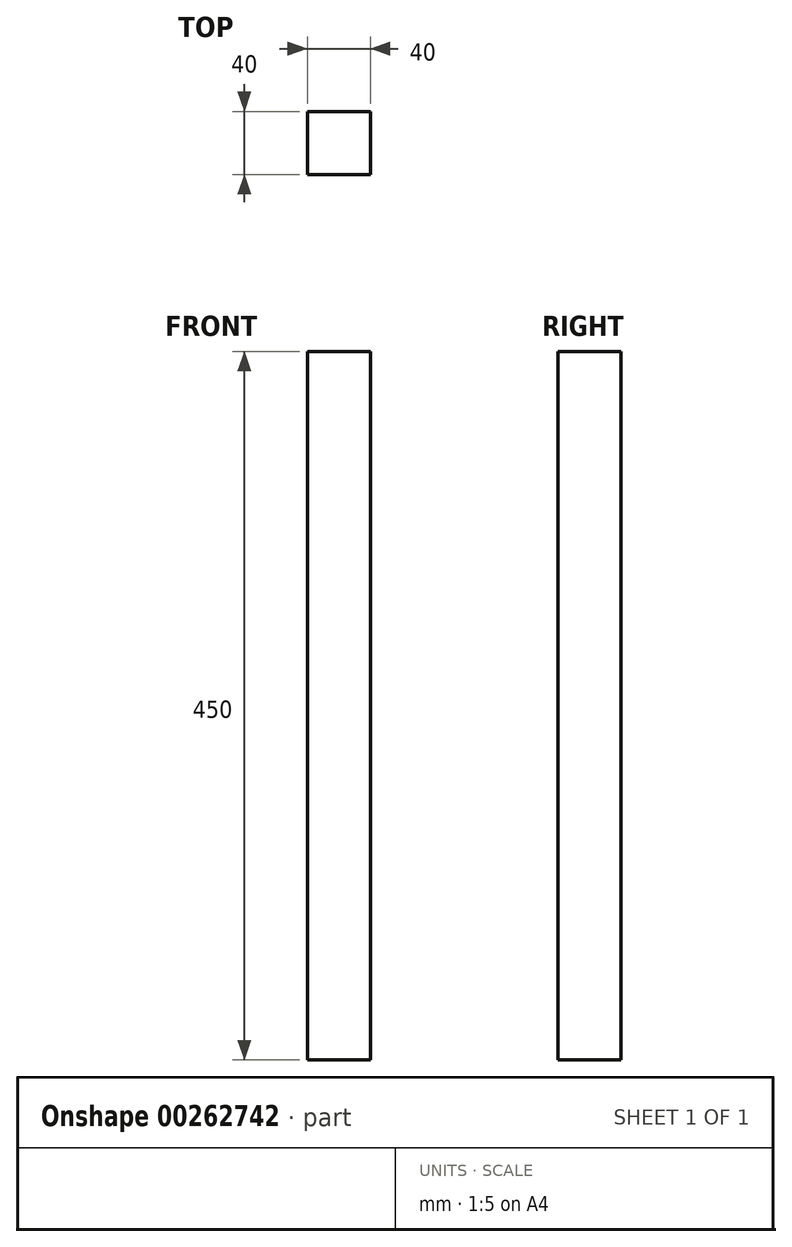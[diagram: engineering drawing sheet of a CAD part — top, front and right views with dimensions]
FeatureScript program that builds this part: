
annotation { "Feature Type Name" : "Feature", "Feature Type Description" : "" }
export const myFeature = defineFeature(function(context is Context, id is Id, definition is map)
    precondition{}
    {
        {
            var Q0;
            Q0=qCreatedBy(makeId("Top.planeOp"),FACE);
            var sketch = newSketch(context, id + "F0", { "sketchPlane" : qUnion([Q0])});
            skLineSegment(sketch, "E0.bottom", {"start": v(0, 0) * mm, "end": v(40, 0) * mm});
            skLineSegment(sketch, "E0.top", {"start": v(0, 40) * mm, "end": v(40, 40) * mm});
            skLineSegment(sketch, "E0.left", {"start": v(0, 0) * mm, "end": v(0, 40) * mm});
            skLineSegment(sketch, "E0.right", {"start": v(40, 0) * mm, "end": v(40, 40) * mm});
            skSolve(sketch);
        }
        {
            var Q0;
            Q0 = qSketchRegion(id + "F0", true);
            extrude(context, id + "F1", {"entities" : qUnion([Q0]), "depth" : 450 * mm});
        }
    });
